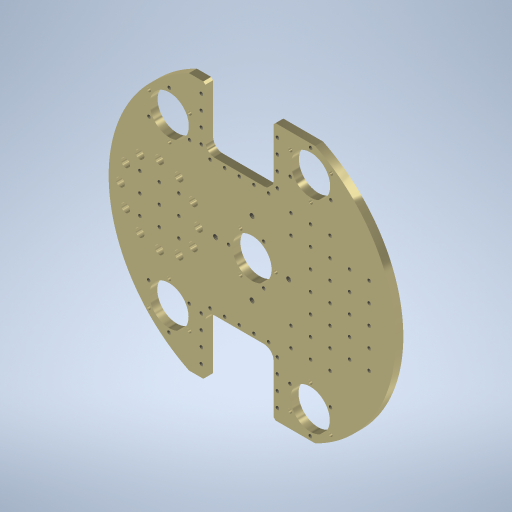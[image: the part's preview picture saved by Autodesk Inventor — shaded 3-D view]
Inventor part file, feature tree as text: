
AUTODESK INVENTOR PART (.ipt)
format: ipt  version: 2024 (Build 280153000, 153)  size: 565,760 bytes
history: native  units: in
note: dims shown in document units (in); Inventor stores cm internally (conversion verified against a paired STEP export)
features: sketch x6, hole x5, extrude x2, chamfer x1
ambient origin geometry x8: Origin, YZ Plane, XZ Plane, XY Plane, X Axis, Y Axis, Z Axis, Center Point
bodies: Solid1 (feature_tree)
feature tree (14):
  extrude  "Extrusion1"  Depth=0.315in TaperAngle=0.0deg
  extrude  "Extrusion2"  Depth=10.3937in
  chamfer  "Chamfer1"  Distance=0.3937in
  hole  "40mm cutouts"  [1 undecoded]
  hole  "Mixing Chamber Mount"  [1 undecoded]
  hole  "M4 mounting holes"  [1 undecoded]
  hole  "M4 clearance holes"  [1 undecoded]
  hole  "M6 mounting holes"  [1 undecoded]
  sketch  "Sketch2"  dims[d0=11.5748in d1=0.315in d2=0.0in]
  sketch  "Sketch4"  dims[d3=10.3937in d4=5.1969in]
  sketch  "Sketch5"  dims[d5=2.7559in]
  sketch  "Sketch6"  dims[d6=2.7559in]
  sketch  "Sketch7"  dims[d7=0.8661in]
  sketch  "Sketch8"  dims[d8=1.8898in d9=0.3937in d10=0.3937in d11=0.3937in d12=0.315in d13=0.0in d14=0.0787in d15=0.0787in d16=45.0deg d18=9.4488in d25=45.0deg d26=30.0deg d27=45.0deg d28=30.0deg d29=1.5748in d30=0.2362in d31=0.1575in d32=0.0787in d33=90.0deg d34=0.315in d35=0.8108in d36=4.7244in d38=360.0deg d40=1.5748in d43=0.3543in d44=0.2362in d45=0.1575in d46=0.0787in d47=90.0deg d48=0.315in d49=0.8108in d50=1.1811in d52=0.7874in d53=1.1811in d55=0.7874in d58=2.9528in d59=0.7874in d60=2.3622in d61=1.5748in d62=1.9685in d64=0.7874in d65=1.5748in d67=0.7874in d71=2.9528in d72=1.0236in d73=0.3543in d74=0.3543in d76=1.9685in d78=0.5906in d79=0.3937in d81=0.3937in d83=1.5748in d85=0.5906in d86=0.3937in d88=0.3937in d90=1.8898in d91=1.8898in d92=1.8898in d93=1.8898in d94=1.8898in d95=1.1811in d97=360.0deg d99=1.1811in d101=360.0deg d103=1.1811in d105=360.0deg d107=1.1811in d109=360.0deg d111=0.1362in d112=0.315in d113=0.1575in d114=0.0787in d115=90.0deg d116=0.4252in d117=0.8108in d122=1.1811in d124=360.0deg d126=1.8898in d127=1.8898in d128=1.8898in d129=1.8898in d130=1.8898in d131=1.1811in d133=360.0deg d135=1.1811in d137=360.0deg d139=1.1811in d141=360.0deg d143=1.1811in d145=360.0deg d147=1.1811in d149=360.0deg d151=0.1654in d152=0.315in d153=0.1575in d154=0.0787in d155=90.0deg d156=0.4252in d157=0.8108in d158=2.9528in d159=1.5748in d161=360.0deg d163=0.1936in d164=0.4724in d165=0.1575in d166=0.0787in d167=90.0deg d168=0.6732in d169=0.8108in]
note: 5 required parameter values undecoded (feature->parameter linkage not recoverable at this tier; creation-order binding heuristic only, values carry confidence <= 0.55)
